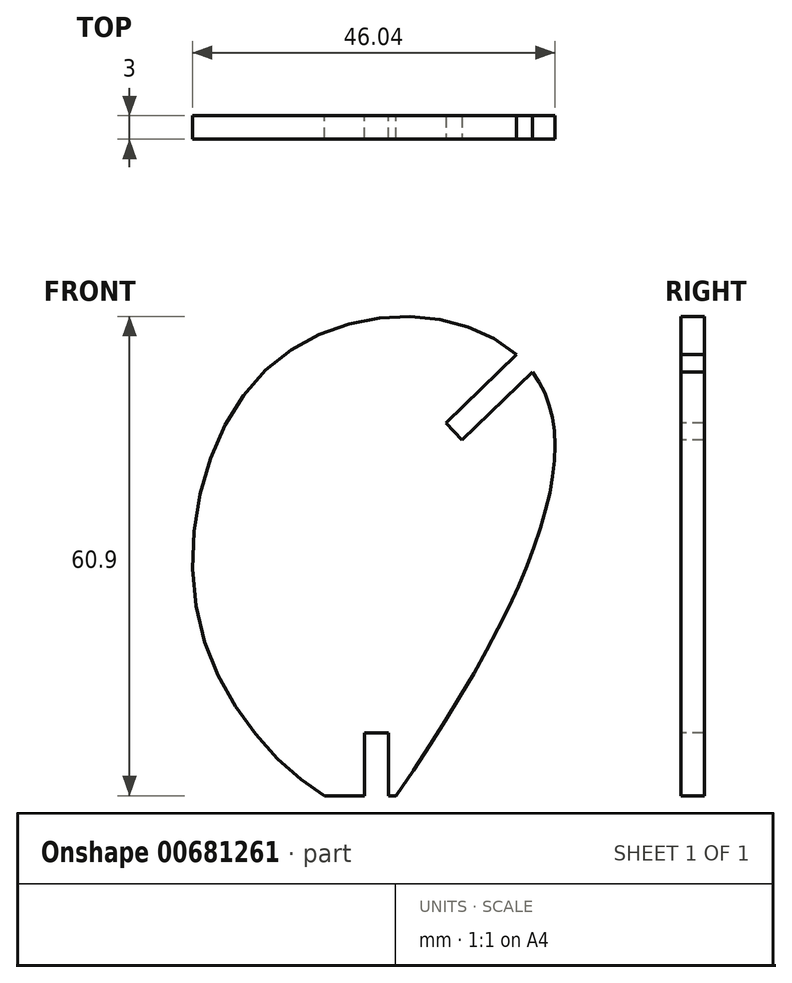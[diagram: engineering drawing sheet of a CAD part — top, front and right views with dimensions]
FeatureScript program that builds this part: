
annotation { "Feature Type Name" : "Feature", "Feature Type Description" : "" }
export const myFeature = defineFeature(function(context is Context, id is Id, definition is map)
    precondition{}
    {
        {
            assignVariable(context, id + "F0", {"name" : "MaterialDepth", "anyValue" : 3 * mm});
        }
        {
            var Q0;
            Q0=qCreatedBy(makeId("Front.planeOp"),FACE);
            var sketch = newSketch(context, id + "F1", { "sketchPlane" : qUnion([Q0])});
            skLineSegment(sketch, "E0", {"start": v(0, 53.6) * mm, "end": v(0, -7.3) * mm, "construction": true});
            skFitSpline(sketch, "E1", {"points": [v(-6.58, 0) * mm, v(-22.5, 22) * mm, v(-15.2, 52.94) * mm, v(6.9, 60.67) * mm, v(21.7, 50.29) * mm, v(2.48, 0) * mm], "startDerivative": vector(-102.35, 61.83) * mm, "endDerivative": vector(-172.56, -250.25) * mm});
            skLineSegment(sketch, "E2", {"start": v(-6.58, 0) * mm, "end": v(2.48, 0) * mm});
            skSolve(sketch);
        }
        {
            var Q0;
            Q0=makeQuery(id+"F1.imprint","IMPRINT",FACE,{"disambiguationData":[TD([[makeQuery(id+"F1.imprint","IMPRINT",EDGE,{"derivedFrom":sQuery(id+"F1.wireOp",EDGE,"E1")}),-1.0]])]});
            extrude(context, id + "F2", {"entities" : qUnion([Q0]), "endBound" : BoundingType.SYMMETRIC, "depth" : getVariable(context, 'MaterialDepth'), "offsetDistance" : 25 * mm});
        }
        {
            var Q0;
            Q0=makeQuery(id+"F2.opExtrude","CAP_FACE",FACE,{"disambiguationData":[OSD([sQuery(id+"F1.wireOp",EDGE,"E1"),sQuery(id+"F1.wireOp",EDGE,"E2")])],"isStart":false});
            var sketch = newSketch(context, id + "F3", { "sketchPlane" : qUnion([Q0])});
            skPoint(sketch, "E3", {"position": v(18.83, 55) * mm});
            skLineSegment(sketch, "E4", {"start": v(18.83, 55) * mm, "end": v(12.2, 48.6) * mm, "construction": true});
            skLineSegment(sketch, "E5", {"start": v(18.83, 55) * mm, "end": v(19.82, 53.97) * mm, "construction": true});
            skLineSegment(sketch, "E6", {"start": v(10.88, 45.22) * mm, "end": v(9.84, 46.3) * mm});
            skLineSegment(sketch, "E7.MirrorCS", {"start": v(28.86, 62.6) * mm, "end": v(27.81, 63.68) * mm});
            skLineSegment(sketch, "E8", {"start": v(10.88, 45.22) * mm, "end": v(28.86, 62.6) * mm});
            skLineSegment(sketch, "E9.MirrorCS", {"start": v(8.8, 47.38) * mm, "end": v(9.84, 46.3) * mm});
            skLineSegment(sketch, "E10.MirrorCS", {"start": v(8.8, 47.38) * mm, "end": v(26.77, 64.76) * mm});
            skLineSegment(sketch, "E11.MirrorCS", {"start": v(26.77, 64.76) * mm, "end": v(27.81, 63.68) * mm});
            skLineSegment(sketch, "E12.bottom", {"start": v(1.5, -8) * mm, "end": v(-1.5, -8) * mm});
            skLineSegment(sketch, "E12.top", {"start": v(1.5, 8) * mm, "end": v(-1.5, 8) * mm});
            skLineSegment(sketch, "E12.left", {"start": v(1.5, -8) * mm, "end": v(1.5, 8) * mm});
            skLineSegment(sketch, "E12.right", {"start": v(-1.5, -8) * mm, "end": v(-1.5, 8) * mm});
            skPoint(sketch, "E12.middle", {"position": v(0, 0) * mm});
            skSolve(sketch);
        }
        {
            var Q0;
            Q0=qSketchRegion(id+"F3",true);
            extrude(context, id + "F4", {"entities" : qUnion([Q0]), "operationType" : NewBodyOperationType.REMOVE, "oppositeDirection" : true, "depth" : 25 * mm, "offsetDistance" : 25 * mm});
        }
    });
